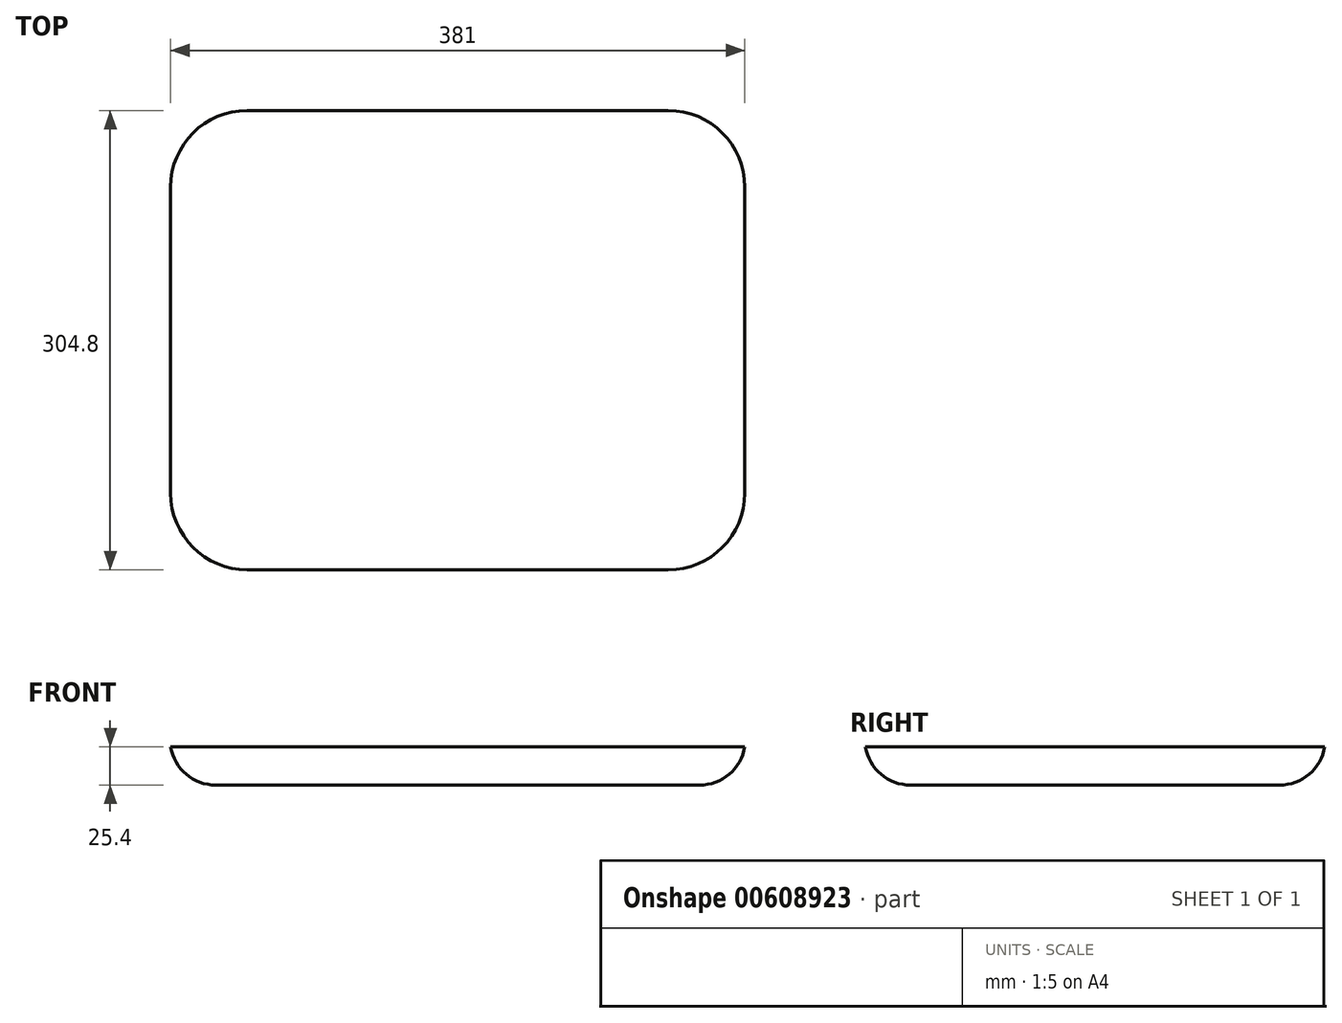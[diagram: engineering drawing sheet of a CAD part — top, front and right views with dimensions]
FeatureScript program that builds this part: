
annotation { "Feature Type Name" : "Feature", "Feature Type Description" : "" }
export const myFeature = defineFeature(function(context is Context, id is Id, definition is map)
    precondition{}
    {
        {
            var Q0;
            Q0=qCreatedBy(makeId("Top.planeOp"),FACE);
            var sketch = newSketch(context, id + "F0", { "sketchPlane" : qUnion([Q0])});
            skLineSegment(sketch, "E0.bottom", {"start": v(139.7, -152.4) * mm, "end": v(-139.7, -152.4) * mm});
            skLineSegment(sketch, "E0.top", {"start": v(139.7, 152.4) * mm, "end": v(-139.7, 152.4) * mm});
            skLineSegment(sketch, "E0.left", {"start": v(190.5, -101.6) * mm, "end": v(190.5, 101.6) * mm});
            skLineSegment(sketch, "E0.right", {"start": v(-190.5, -101.6) * mm, "end": v(-190.5, 101.6) * mm});
            skPoint(sketch, "E0.middle", {"position": v(0, 0) * mm});
            skPoint(sketch, "E1.visualSharp", {"position": v(-190.5, 152.4) * mm});
            skArc(sketch, "E1.filletArc", {"start": v(-139.7, 152.4) * mm, "mid": v(-175.62, 137.52) * mm, "end": v(-190.5, 101.6) * mm});
            skPoint(sketch, "E2.visualSharp", {"position": v(190.5, 152.4) * mm});
            skArc(sketch, "E2.filletArc", {"start": v(190.5, 101.6) * mm, "mid": v(175.62, 137.52) * mm, "end": v(139.7, 152.4) * mm});
            skPoint(sketch, "E3.visualSharp", {"position": v(190.5, -152.4) * mm});
            skArc(sketch, "E3.filletArc", {"start": v(139.7, -152.4) * mm, "mid": v(175.62, -137.52) * mm, "end": v(190.5, -101.6) * mm});
            skPoint(sketch, "E4.visualSharp", {"position": v(-190.5, -152.4) * mm});
            skArc(sketch, "E4.filletArc", {"start": v(-190.5, -101.6) * mm, "mid": v(-175.62, -137.52) * mm, "end": v(-139.7, -152.4) * mm});
            skSolve(sketch);
        }
        {
            var Q0;
            Q0=makeQuery(id+"F0.imprint","IMPRINT",FACE,{"disambiguationData":[TD([[makeQuery(id+"F0.imprint","IMPRINT",EDGE,{"derivedFrom":sQuery(id+"F0.wireOp",EDGE,"E0.bottom")}),-1.0]])]});
            extrude(context, id + "F1", {"entities" : qUnion([Q0]), "depth" : 25.4 * mm, "offsetDistance" : 25.4 * mm});
        }
        {
            var Q0;
            Q0=makeQuery(id+"F1.opExtrude","CAP_EDGE",EDGE,{"disambiguationData":[OSD([sQuery(id+"F0.wireOp",EDGE,"E0.bottom")])],"isStart":true});
            fillet(context, id + "F2", {"entities" : qUnion([Q0]), "radius" : 30.48 * mm, "tangentPropagation" : true, "allowEdgeOverflow" : false});
        }
    });
